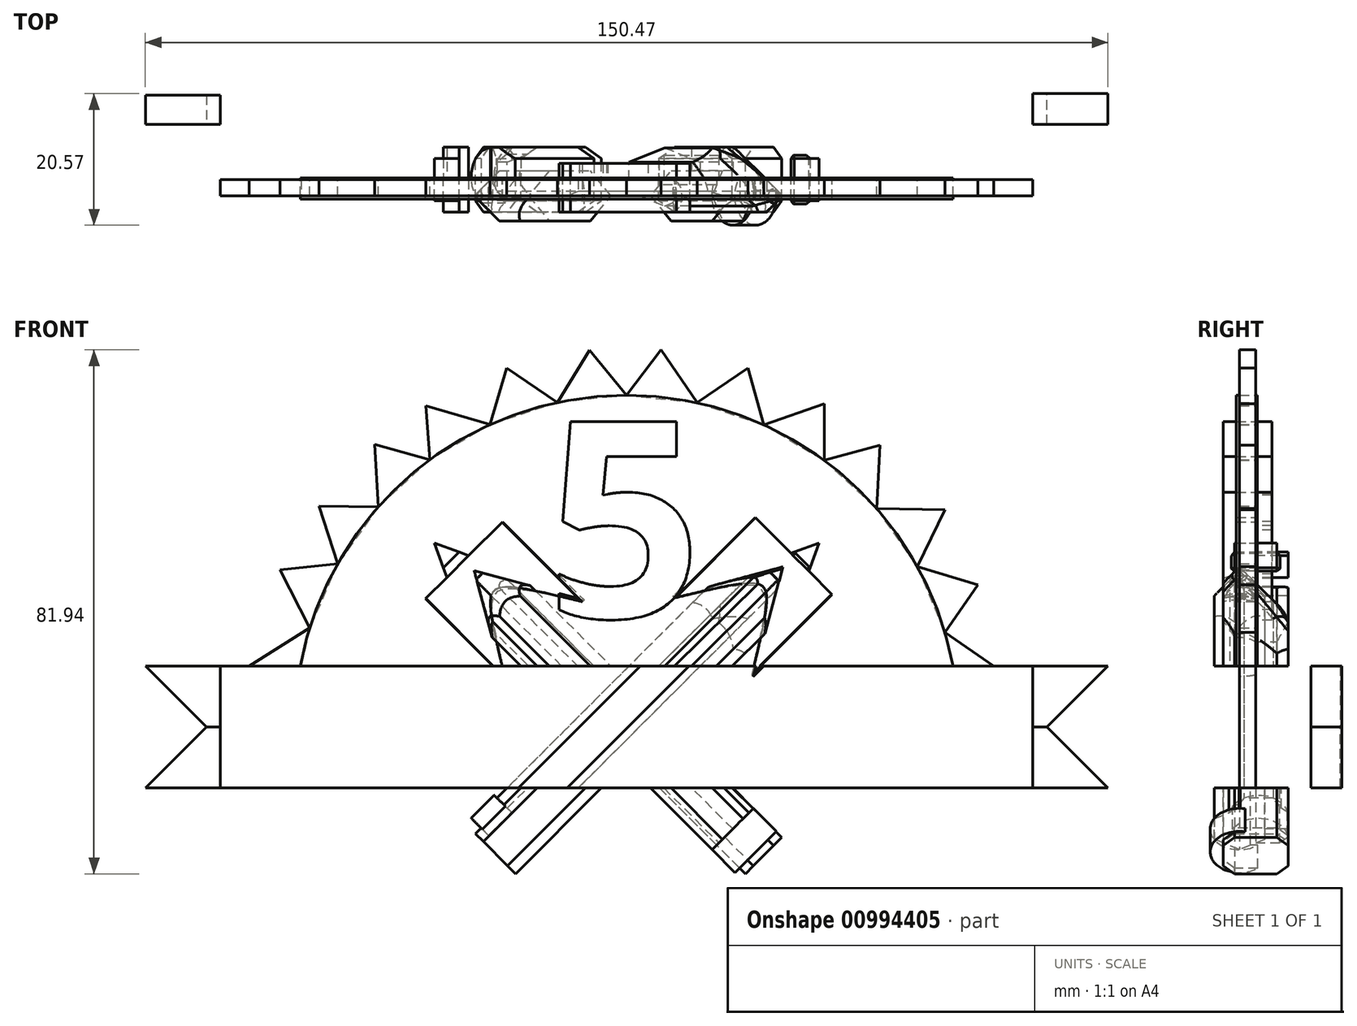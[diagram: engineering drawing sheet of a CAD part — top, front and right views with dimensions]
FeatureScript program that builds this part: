
annotation { "Feature Type Name" : "Feature", "Feature Type Description" : "" }
export const myFeature = defineFeature(function(context is Context, id is Id, definition is map)
    precondition{}
    {
        {
            var Q0;
            Q0=qCreatedBy(makeId("Front.planeOp"),FACE);
            var sketch = newSketch(context, id + "F0", { "sketchPlane" : qUnion([Q0])});
            skLineSegment(sketch, "E0.bottom", {"start": v(-63.5, 9.53) * mm, "end": v(63.5, 9.53) * mm});
            skLineSegment(sketch, "E0.top", {"start": v(-63.5, -9.52) * mm, "end": v(63.5, -9.52) * mm});
            skLineSegment(sketch, "E0.left", {"start": v(-63.5, 9.53) * mm, "end": v(-63.5, -9.52) * mm});
            skLineSegment(sketch, "E0.right", {"start": v(63.5, 9.53) * mm, "end": v(63.5, -9.52) * mm});
            skSolve(sketch);
        }
        {
            var Q0;
            Q0=qCreatedBy(makeId("Top.planeOp"),FACE);
            var sketch = newSketch(context, id + "F1", { "sketchPlane" : qUnion([Q0])});
            skLineSegment(sketch, "E1", {"start": v(-63.5, 0) * mm, "end": v(-57.46, 8.63) * mm});
            skLineSegment(sketch, "E2", {"start": v(-57.46, 8.63) * mm, "end": v(-42.22, 8.63) * mm});
            skLineSegment(sketch, "E3", {"start": v(-42.22, 8.63) * mm, "end": v(-48.26, 0) * mm});
            skLineSegment(sketch, "E4", {"start": v(-48.26, 0) * mm, "end": v(-63.5, 0) * mm});
            skSolve(sketch);
        }
        {
            var Q0;
            Q0=makeQuery(id+"F1.imprint","IMPRINT",FACE,{"disambiguationData":[TD([[makeQuery(id+"F1.imprint","IMPRINT",EDGE,{"derivedFrom":sQuery(id+"F1.wireOp",EDGE,"E1")}),-1.0]])]});
            extrude(context, id + "F2", {"entities" : qUnion([Q0]), "depth" : 9.52 * mm, "offsetDistance" : 25.4 * mm});
        }
        {
            var Q0;
            Q0=makeQuery(id+"F2.opExtrude","CAP_FACE",FACE,{"disambiguationData":[OSD([sQuery(id+"F1.wireOp",EDGE,"E1"),sQuery(id+"F1.wireOp",EDGE,"E2"),sQuery(id+"F1.wireOp",EDGE,"E3"),sQuery(id+"F1.wireOp",EDGE,"E4")])],"isStart":true});
            extrude(context, id + "F3", {"entities" : qUnion([Q0]), "depth" : 9.52 * mm, "offsetDistance" : 25.4 * mm});
        }
        {
            var Q0;
            Q0=qCreatedBy(makeId("Top.planeOp"),FACE);
            var sketch = newSketch(context, id + "F4", { "sketchPlane" : qUnion([Q0])});
            skLineSegment(sketch, "E5", {"start": v(63.5, 0) * mm, "end": v(57.45, 8.64) * mm});
            skLineSegment(sketch, "E6", {"start": v(57.45, 8.64) * mm, "end": v(42.21, 8.64) * mm});
            skLineSegment(sketch, "E7", {"start": v(42.21, 8.64) * mm, "end": v(48.26, 0) * mm});
            skLineSegment(sketch, "E8", {"start": v(48.26, 0) * mm, "end": v(63.5, 0) * mm});
            skSolve(sketch);
        }
        {
            var Q0;
            Q0 = qSketchRegion(id + "F4", true);
            extrude(context, id + "F5", {"entities" : qUnion([Q0]), "depth" : 9.52 * mm, "offsetDistance" : 25.4 * mm});
        }
        {
            var Q0;
            Q0=makeQuery(id+"F5.opExtrude","CAP_FACE",FACE,{"disambiguationData":[OSD([sQuery(id+"F4.wireOp",EDGE,"E5"),sQuery(id+"F4.wireOp",EDGE,"E6"),sQuery(id+"F4.wireOp",EDGE,"E7"),sQuery(id+"F4.wireOp",EDGE,"E8")])],"isStart":true});
            var Q1;
            Q1 = qSketchRegion(id + "F3emU6Rc3k6mnXg_5", true);
            extrude(context, id + "F6", {"entities" : qUnion([Q0, Q1]), "depth" : 9.52 * mm, "offsetDistance" : 25.4 * mm});
        }
        {
            var Q0;
            Q0=qCreatedBy(makeId("Front.planeOp"),FACE);
            var sketch = newSketch(context, id + "F7", { "sketchPlane" : qUnion([Q0])});
            skLineSegment(sketch, "E9", {"start": v(0, 0) * mm, "end": v(0, 56.19) * mm, "construction": true});
            skSolve(sketch);
        }
        {
            var Q0;
            Q0=makeQuery(id+"F0.imprint","IMPRINT",FACE,{"disambiguationData":[TD([[makeQuery(id+"F0.imprint","IMPRINT",EDGE,{"derivedFrom":sQuery(id+"F0.wireOp",EDGE,"E0.bottom")}),-1.0]])]});
            var sketch = newSketch(context, id + "F8", { "sketchPlane" : qUnion([Q0])});
            skArc(sketch, "E10", {"start": v(51.02, 9.53) * mm, "mid": v(0, 51.9) * mm, "end": v(-51.02, 9.52) * mm});
            skSolve(sketch);
        }
        {
            var Q0;
            {var subQ0=sQuery(id+"F8.wireOp",EDGE,"E10");Q0=makeQuery(id+"F8.imprint","IMPRINT",FACE,{"disambiguationData":[TD([[makeQuery(id+"F8.imprint","IMPRINT",EDGE,{"derivedFrom":subQ0}),1.0]])]});}
            extrude(context, id + "F9", {"entities" : qUnion([Q0]), "oppositeDirection" : true, "depth" : 0.25 * mm, "offsetDistance" : 25.4 * mm});
        }
        {
            var Q0;
            Q0=qCreatedBy(makeId("Front.planeOp"),FACE);
            var sketch = newSketch(context, id + "F10", { "sketchPlane" : qUnion([Q0])});
            skText(sketch, "E11", { "text": "5\n", "fontName": "OpenSans-Bold.ttf"});
            const initialGuessF10  = {"E11": [-0.01267, 0.01715, 1, 0, 0.03088]};
            skSetInitialGuess(sketch, initialGuessF10);
            skSolve(sketch);
        }
        {
            var Q0;
            Q0 = qSketchRegion(id + "F10", true);
            extrude(context, id + "F11", {"entities" : qUnion([Q0]), "depth" : 5.08 * mm, "offsetDistance" : 25.4 * mm});
        }
        {
            var Q0;
            Q0=qCreatedBy(makeId("Front.planeOp"),FACE);
            var sketch = newSketch(context, id + "F12", { "sketchPlane" : qUnion([Q0])});
            skText(sketch, "E12", { "text": "SoHacks", "fontName": "OpenSans-Bold.ttf"});
            const initialGuessF12  = {"E12": [-0.03987, -0.0065, 1, 0, 0.01368]};
            skSetInitialGuess(sketch, initialGuessF12);
            skSolve(sketch);
        }
        {
            var Q0;
            Q0 = qSketchRegion(id + "F12", true);
            extrude(context, id + "F13", {"entities" : qUnion([Q0]), "depth" : 5.08 * mm, "offsetDistance" : 25.4 * mm});
        }
        {
            var Q0;
            Q0=qCreatedBy(makeId("Top.planeOp"),FACE);
            var sketch = newSketch(context, id + "F14", { "sketchPlane" : qUnion([Q0])});
            skLineSegment(sketch, "E13.bottom", {"start": v(-42.22, 8.63) * mm, "end": v(-75.24, 8.63) * mm});
            skLineSegment(sketch, "E13.top", {"start": v(-42.22, 13.2) * mm, "end": v(-75.24, 13.2) * mm});
            skLineSegment(sketch, "E13.left", {"start": v(-42.22, 8.63) * mm, "end": v(-42.22, 13.2) * mm});
            skLineSegment(sketch, "E13.right", {"start": v(-75.24, 8.63) * mm, "end": v(-75.24, 13.2) * mm});
            skSolve(sketch);
        }
        {
            var Q0;
            Q0 = qSketchRegion(id + "F14", true);
            extrude(context, id + "F15", {"entities" : qUnion([Q0]), "depth" : 9.52 * mm, "offsetDistance" : 25.4 * mm});
        }
        {
            var Q0;
            Q0=makeQuery(id+"F15.opExtrude","CAP_FACE",FACE,{"disambiguationData":[OSD([sQuery(id+"F14.wireOp",EDGE,"E13.bottom"),sQuery(id+"F14.wireOp",EDGE,"E13.top"),sQuery(id+"F14.wireOp",EDGE,"E13.left"),sQuery(id+"F14.wireOp",EDGE,"E13.right")])],"isStart":true});
            extrude(context, id + "F16", {"entities" : qUnion([Q0]), "depth" : 9.52 * mm, "offsetDistance" : 25.4 * mm});
        }
        {
            var Q0;
            Q0=makeQuery(id+"F15.opExtrude","CAP_EDGE",EDGE,{"disambiguationData":[OSD([sQuery(id+"F14.wireOp",EDGE,"E13.right")])],"isStart":true});
            chamfer(context, id + "F17", {"entities" : qUnion([Q0]), "width" : 9.52 * mm, "tangentPropagation" : true});
        }
        {
            var Q0;
            Q0=makeQuery(id+"F16.opExtrude","CAP_EDGE",EDGE,{"disambiguationData":[OSD([sQuery(id+"F14.wireOp",EDGE,"E13.right")])],"isStart":true});
            chamfer(context, id + "F18", {"entities" : qUnion([Q0]), "width" : 9.52 * mm, "tangentPropagation" : true});
        }
        {
            var Q0;
            Q0=qCreatedBy(makeId("Top.planeOp"),FACE);
            var sketch = newSketch(context, id + "F19", { "sketchPlane" : qUnion([Q0])});
            skLineSegment(sketch, "E14.bottom", {"start": v(42.21, 8.64) * mm, "end": v(75.23, 8.64) * mm});
            skLineSegment(sketch, "E14.top", {"start": v(42.21, 13.46) * mm, "end": v(75.23, 13.46) * mm});
            skLineSegment(sketch, "E14.left", {"start": v(42.21, 8.64) * mm, "end": v(42.21, 13.46) * mm});
            skLineSegment(sketch, "E14.right", {"start": v(75.23, 8.64) * mm, "end": v(75.23, 13.46) * mm});
            skSolve(sketch);
        }
        {
            var Q0;
            Q0=makeQuery(id+"F19.imprint","IMPRINT",FACE,{"disambiguationData":[TD([[makeQuery(id+"F19.imprint","IMPRINT",EDGE,{"derivedFrom":sQuery(id+"F19.wireOp",EDGE,"E14.bottom")}),1.0]])]});
            extrude(context, id + "F20", {"entities" : qUnion([Q0]), "depth" : 9.52 * mm, "offsetDistance" : 25.4 * mm});
        }
        {
            var Q0;
            Q0 = qSketchRegion(id + "F19", true);
            extrude(context, id + "F21", {"entities" : qUnion([Q0]), "oppositeDirection" : true, "depth" : 9.52 * mm, "offsetDistance" : 25.4 * mm});
        }
        {
            var Q0;
            Q0=makeQuery(id+"F20.opExtrude","CAP_EDGE",EDGE,{"disambiguationData":[OSD([sQuery(id+"F19.wireOp",EDGE,"E14.right")])],"isStart":true});
            chamfer(context, id + "F22", {"entities" : qUnion([Q0]), "width" : 9.52 * mm, "tangentPropagation" : true});
        }
        {
            var Q0;
            Q0=makeQuery(id+"F21.opExtrude","CAP_EDGE",EDGE,{"disambiguationData":[OSD([sQuery(id+"F19.wireOp",EDGE,"E14.right")])],"isStart":true});
            chamfer(context, id + "F23", {"entities" : qUnion([Q0]), "width" : 9.52 * mm, "tangentPropagation" : true});
        }
        {
            var Q0;
            Q0=qCreatedBy(makeId("Front.planeOp"),FACE);
            var sketch = newSketch(context, id + "F24", { "sketchPlane" : qUnion([Q0])});
            skLineSegment(sketch, "E15", {"start": v(0, 0) * mm, "end": v(0, 9.53) * mm, "construction": true});
            skLineSegment(sketch, "E16", {"start": v(0, 9.53) * mm, "end": v(-10.16, 9.53) * mm, "construction": true});
            skLineSegment(sketch, "E17", {"start": v(0, 9.53) * mm, "end": v(10.16, 9.53) * mm, "construction": true});
            skLineSegment(sketch, "E18", {"start": v(-10.16, 9.53) * mm, "end": v(-16.51, 9.53) * mm, "construction": true});
            skLineSegment(sketch, "E19", {"start": v(10.16, 9.53) * mm, "end": v(16.51, 9.53) * mm, "construction": true});
            skLineSegment(sketch, "E20", {"start": v(0, 0) * mm, "end": v(0, -9.52) * mm, "construction": true});
            skLineSegment(sketch, "E21", {"start": v(0, -9.52) * mm, "end": v(-10.16, -9.52) * mm, "construction": true});
            skLineSegment(sketch, "E22", {"start": v(-10.16, -9.52) * mm, "end": v(-16.51, -9.52) * mm, "construction": true});
            skLineSegment(sketch, "E23", {"start": v(0, -9.52) * mm, "end": v(10.16, -9.52) * mm, "construction": true});
            skLineSegment(sketch, "E24", {"start": v(10.16, -9.52) * mm, "end": v(16.51, -9.52) * mm, "construction": true});
            skSolve(sketch);
        }
        {
            var Q0;
            Q0=qCreatedBy(makeId("Front.planeOp"),FACE);
            var sketch = newSketch(context, id + "F25", { "sketchPlane" : qUnion([Q0])});
            skLineSegment(sketch, "E25", {"start": v(-10.16, 9.52) * mm, "end": v(-23.63, 23) * mm});
            skLineSegment(sketch, "E26", {"start": v(-23.63, 23) * mm, "end": v(-26.8, 19.82) * mm});
            skLineSegment(sketch, "E27", {"start": v(-26.8, 19.82) * mm, "end": v(-16.51, 9.52) * mm});
            skLineSegment(sketch, "E28", {"start": v(10.16, 9.52) * mm, "end": v(23.63, 23) * mm});
            skLineSegment(sketch, "E29", {"start": v(23.63, 23) * mm, "end": v(26.8, 19.82) * mm});
            skLineSegment(sketch, "E30", {"start": v(26.8, 19.82) * mm, "end": v(16.5, 9.53) * mm});
            skLineSegment(sketch, "E31", {"start": v(-10.16, 9.52) * mm, "end": v(-16.51, 9.52) * mm});
            skLineSegment(sketch, "E32", {"start": v(10.16, 9.52) * mm, "end": v(16.5, 9.53) * mm});
            skSolve(sketch);
        }
        {
            var Q0;
            Q0 = qSketchRegion(id + "F25", true);
            extrude(context, id + "F26", {"entities" : qUnion([Q0]), "depth" : 5.08 * mm, "offsetDistance" : 25.4 * mm});
        }
        {
            var Q0;
            Q0=qCreatedBy(makeId("Front.planeOp"),FACE);
            var sketch = newSketch(context, id + "F27", { "sketchPlane" : qUnion([Q0])});
            skLineSegment(sketch, "E33", {"start": v(23.63, 23) * mm, "end": v(21.13, 25.52) * mm});
            skLineSegment(sketch, "E34", {"start": v(21.13, 25.52) * mm, "end": v(4.97, 9.52) * mm});
            skLineSegment(sketch, "E35", {"start": v(4.97, 9.53) * mm, "end": v(10.16, 9.53) * mm});
            skLineSegment(sketch, "E36", {"start": v(10.16, 9.52) * mm, "end": v(23.63, 23) * mm});
            skLineSegment(sketch, "E37", {"start": v(-23.63, 23) * mm, "end": v(-21.12, 25.5) * mm});
            skLineSegment(sketch, "E38", {"start": v(-21.12, 25.5) * mm, "end": v(-5.13, 9.52) * mm});
            skLineSegment(sketch, "E39", {"start": v(-5.13, 9.53) * mm, "end": v(-10.16, 9.53) * mm});
            skLineSegment(sketch, "E40", {"start": v(-10.16, 9.52) * mm, "end": v(-23.63, 23) * mm});
            skSolve(sketch);
        }
        {
            var Q0;
            Q0 = qSketchRegion(id + "F27", true);
            extrude(context, id + "F28", {"entities" : qUnion([Q0]), "depth" : 5.08 * mm, "offsetDistance" : 25.4 * mm});
        }
        {
            var Q0;
            Q0=qCreatedBy(makeId("Front.planeOp"),FACE);
            var sketch = newSketch(context, id + "F29", { "sketchPlane" : qUnion([Q0])});
            skLineSegment(sketch, "E41", {"start": v(-26.8, 19.82) * mm, "end": v(-30.06, 28.77) * mm, "construction": true});
            skLineSegment(sketch, "E42", {"start": v(-30.06, 28.77) * mm, "end": v(-21.12, 25.5) * mm, "construction": true});
            skLineSegment(sketch, "E43", {"start": v(-21.12, 25.5) * mm, "end": v(-26.8, 19.82) * mm, "construction": true});
            skLineSegment(sketch, "E44", {"start": v(21.13, 25.52) * mm, "end": v(26.8, 19.82) * mm, "construction": true});
            skLineSegment(sketch, "E45", {"start": v(26.8, 19.82) * mm, "end": v(30.08, 28.76) * mm, "construction": true});
            skLineSegment(sketch, "E46", {"start": v(30.08, 28.76) * mm, "end": v(21.13, 25.52) * mm, "construction": true});
            skSolve(sketch);
        }
        {
            var Q0;
            Q0=qCreatedBy(makeId("Front.planeOp"),FACE);
            var sketch = newSketch(context, id + "F30", { "sketchPlane" : qUnion([Q0])});
            skLineSegment(sketch, "E47", {"start": v(21.13, 25.52) * mm, "end": v(26.2, 27.36) * mm});
            skLineSegment(sketch, "E48", {"start": v(26.2, 27.36) * mm, "end": v(28.66, 24.9) * mm});
            skLineSegment(sketch, "E49", {"start": v(28.66, 24.9) * mm, "end": v(26.8, 19.82) * mm});
            skLineSegment(sketch, "E50", {"start": v(26.8, 19.82) * mm, "end": v(21.13, 25.52) * mm});
            skLineSegment(sketch, "E51", {"start": v(-26.8, 19.82) * mm, "end": v(-21.12, 25.5) * mm});
            skLineSegment(sketch, "E52", {"start": v(-21.12, 25.5) * mm, "end": v(-26.2, 27.36) * mm});
            skLineSegment(sketch, "E53", {"start": v(-26.2, 27.36) * mm, "end": v(-28.65, 24.9) * mm});
            skLineSegment(sketch, "E54", {"start": v(-28.65, 24.9) * mm, "end": v(-26.8, 19.82) * mm});
            skSolve(sketch);
        }
        {
            var Q0;
            Q0 = qSketchRegion(id + "F30", true);
            extrude(context, id + "F31", {"entities" : qUnion([Q0]), "depth" : 5.08 * mm, "offsetDistance" : 25.4 * mm});
        }
        {
            var Q0;
            Q0=qCreatedBy(makeId("Front.planeOp"),FACE);
            var sketch = newSketch(context, id + "F32", { "sketchPlane" : qUnion([Q0])});
            skLineSegment(sketch, "E55", {"start": v(26.2, 27.36) * mm, "end": v(28.66, 24.9) * mm});
            skLineSegment(sketch, "E56", {"start": v(28.66, 24.9) * mm, "end": v(30.08, 28.76) * mm});
            skLineSegment(sketch, "E57", {"start": v(30.08, 28.76) * mm, "end": v(26.2, 27.36) * mm});
            skLineSegment(sketch, "E58", {"start": v(-28.65, 24.9) * mm, "end": v(-26.2, 27.36) * mm});
            skLineSegment(sketch, "E59", {"start": v(-26.2, 27.36) * mm, "end": v(-30.06, 28.77) * mm});
            skLineSegment(sketch, "E60", {"start": v(-30.06, 28.77) * mm, "end": v(-28.65, 24.9) * mm});
            skSolve(sketch);
        }
        {
            var Q0;
            Q0 = qSketchRegion(id + "F32", true);
            extrude(context, id + "F33", {"entities" : qUnion([Q0]), "depth" : 3.3 * mm, "offsetDistance" : 25.4 * mm});
        }
        {
            var Q0;
            Q0=qCreatedBy(makeId("Front.planeOp"),FACE);
            var sketch = newSketch(context, id + "F34", { "sketchPlane" : qUnion([Q0])});
            skLineSegment(sketch, "E61", {"start": v(16.51, -9.52) * mm, "end": v(24.25, -17.26) * mm});
            skLineSegment(sketch, "E62", {"start": v(24.25, -17.26) * mm, "end": v(21.07, -20.44) * mm});
            skLineSegment(sketch, "E63", {"start": v(21.07, -20.44) * mm, "end": v(10.16, -9.52) * mm});
            skLineSegment(sketch, "E64", {"start": v(10.16, -9.52) * mm, "end": v(16.51, -9.52) * mm});
            skLineSegment(sketch, "E65", {"start": v(-16.52, -9.52) * mm, "end": v(-10.16, -9.52) * mm});
            skLineSegment(sketch, "E66", {"start": v(-10.16, -9.52) * mm, "end": v(-20.48, -19.85) * mm});
            skLineSegment(sketch, "E67", {"start": v(-20.48, -19.85) * mm, "end": v(-23.66, -16.67) * mm});
            skLineSegment(sketch, "E68", {"start": v(-23.66, -16.67) * mm, "end": v(-16.52, -9.52) * mm});
            skSolve(sketch);
        }
        {
            var Q0;
            Q0 = qSketchRegion(id + "F34", true);
            extrude(context, id + "F35", {"entities" : qUnion([Q0]), "depth" : 5.08 * mm, "offsetDistance" : 25.4 * mm});
        }
        {
            var Q0;
            Q0=qCreatedBy(makeId("Front.planeOp"),FACE);
            var sketch = newSketch(context, id + "F36", { "sketchPlane" : qUnion([Q0])});
            skLineSegment(sketch, "E69", {"start": v(-20.48, -19.85) * mm, "end": v(-17.38, -22.95) * mm});
            skLineSegment(sketch, "E70", {"start": v(-17.38, -22.95) * mm, "end": v(-3.95, -9.52) * mm});
            skLineSegment(sketch, "E71", {"start": v(-3.95, -9.52) * mm, "end": v(-10.16, -9.52) * mm});
            skLineSegment(sketch, "E72", {"start": v(-10.16, -9.53) * mm, "end": v(-20.48, -19.85) * mm});
            skLineSegment(sketch, "E73", {"start": v(10.16, -9.52) * mm, "end": v(5.13, -9.52) * mm});
            skLineSegment(sketch, "E74", {"start": v(5.13, -9.52) * mm, "end": v(18.56, -22.95) * mm});
            skLineSegment(sketch, "E75", {"start": v(18.56, -22.95) * mm, "end": v(21.07, -20.44) * mm});
            skLineSegment(sketch, "E76", {"start": v(21.07, -20.44) * mm, "end": v(10.16, -9.52) * mm});
            skSolve(sketch);
        }
        {
            var Q0;
            Q0=makeQuery(id+"F35.opExtrude","SWEPT_FACE",FACE,{"disambiguationData":[OSD([sQuery(id+"F34.wireOp",EDGE,"E62")])]});
            cPlane(context, id + "F37", {"entities" : qUnion([Q0]), "cplaneType" : CPlaneType.OFFSET, "offset" : 0 * mm, "width" : 152.4 * mm, "height" : 152.4 * mm});
        }
        {
            var Q0;
            Q0=qCreatedBy(id+"F37.planeOp",FACE);
            var sketch = newSketch(context, id + "F38", { "sketchPlane" : qUnion([Q0])});
            skCircle(sketch, "E77.cCircle", {"center": v(-2.54, 0.45) * mm, "radius": 3.94 * mm, "construction": true});
            skLineSegment(sketch, "E77.0", {"start": v(-6.48, 2.72) * mm, "end": v(-2.54, 5) * mm});
            skLineSegment(sketch, "E77.1", {"start": v(-2.54, 5) * mm, "end": v(1.4, 2.72) * mm});
            skLineSegment(sketch, "E77.2", {"start": v(1.4, 2.72) * mm, "end": v(1.4, -1.82) * mm});
            skLineSegment(sketch, "E77.3", {"start": v(1.4, -1.82) * mm, "end": v(-2.54, -4.1) * mm});
            skLineSegment(sketch, "E77.4", {"start": v(-2.54, -4.1) * mm, "end": v(-6.48, -1.82) * mm});
            skLineSegment(sketch, "E77.5", {"start": v(-6.48, -1.82) * mm, "end": v(-6.48, 2.72) * mm});
            skPoint(sketch, "E77.0.midPoint", {"position": v(-4.5, 3.86) * mm});
            skSolve(sketch);
        }
        {
            var Q0;
            Q0=makeQuery(id+"F38.imprint","IMPRINT",FACE,{"disambiguationData":[TD([[makeQuery(id+"F38.imprint","IMPRINT",EDGE,{"derivedFrom":sQuery(id+"F38.wireOp",EDGE,"E77.0")}),-1.0]])]});
            extrude(context, id + "F39", {"entities" : qUnion([Q0]), "oppositeDirection" : true, "depth" : 63.5 * mm, "offsetDistance" : 25.4 * mm, "hasSecondDirection" : true, "secondDirectionOppositeDirection" : true, "secondDirectionDepth" : 6.35 * mm});
        }
        {
            var Q0;
            Q0=makeQuery(id+"F39.opExtrude","SWEPT_FACE",FACE,{"disambiguationData":[OSD([sQuery(id+"F38.wireOp",EDGE,"E77.2")])]});
            var Q1;
            Q1=makeQuery(id+"F39.opExtrude","SWEPT_FACE",FACE,{"disambiguationData":[OSD([sQuery(id+"F38.wireOp",EDGE,"E77.5")])]});
            cPlane(context, id + "F40", {"entities" : qUnion([Q0, Q1]), "cplaneType" : CPlaneType.MID_PLANE, "offset" : 25.4 * mm, "oppositeDirection" : true, "width" : 152.4 * mm, "height" : 152.4 * mm});
        }
        {
            var Q0;
            Q0=qCreatedBy(id+"F40.planeOp",FACE);
            var sketch = newSketch(context, id + "F41", { "sketchPlane" : qUnion([Q0])});
            skLineSegment(sketch, "E78", {"start": v(23.83, 24.46) * mm, "end": v(6.65, 19.86) * mm});
            skLineSegment(sketch, "E79", {"start": v(6.65, 19.86) * mm, "end": v(19.16, 32.36) * mm});
            skLineSegment(sketch, "E80", {"start": v(25.44, 26.08) * mm, "end": v(19.16, 32.36) * mm});
            skLineSegment(sketch, "E81", {"start": v(23.83, 24.46) * mm, "end": v(16.64, 17.28) * mm, "construction": true});
            skLineSegment(sketch, "E82", {"start": v(25.44, 26.08) * mm, "end": v(23.83, 24.46) * mm});
            skSolve(sketch);
        }
        {
            var Q0;
            Q0=makeQuery(id+"F41.imprint","IMPRINT",FACE,{"disambiguationData":[TD([[makeQuery(id+"F41.imprint","IMPRINT",EDGE,{"derivedFrom":sQuery(id+"F41.wireOp",EDGE,"E78")}),-1.0]])]});
            var Q1;
            Q1=sQuery(id+"F41.wireOp",EDGE,"E81");
            revolve(context, id + "F42", {"operationType" : NewBodyOperationType.REMOVE, "surfaceOperationType" : NewSurfaceOperationType.NEW, "entities" : qUnion([Q0]), "axis" : qUnion([Q1]), "revolveType" : RevolveType.FULL, "oppositeDirection" : true});
        }
        {
            var Q0;
            Q0 = qSketchRegion(id + "F36", true);
            extrude(context, id + "F43", {"entities" : qUnion([Q0]), "depth" : 5.08 * mm, "offsetDistance" : 25.4 * mm});
        }
        {
            var Q0;
            Q0=qCreatedBy(makeId("Front.planeOp"),FACE);
            var sketch = newSketch(context, id + "F44", { "sketchPlane" : qUnion([Q0])});
            skLineSegment(sketch, "E83", {"start": v(0, 51.9) * mm, "end": v(-10.8, 50.77) * mm});
            skLineSegment(sketch, "E84", {"start": v(-10.8, 50.77) * mm, "end": v(-21.34, 47.31) * mm});
            skLineSegment(sketch, "E85", {"start": v(-21.34, 47.31) * mm, "end": v(-30.77, 41.8) * mm});
            skLineSegment(sketch, "E86", {"start": v(-30.77, 41.8) * mm, "end": v(-38.83, 34.43) * mm});
            skLineSegment(sketch, "E87", {"start": v(-38.83, 34.43) * mm, "end": v(-45.18, 25.54) * mm});
            skLineSegment(sketch, "E88", {"start": v(-45.18, 25.54) * mm, "end": v(-49.52, 15.52) * mm});
            skLineSegment(sketch, "E89", {"start": v(-49.52, 15.52) * mm, "end": v(-50.93, 9.33) * mm});
            skLineSegment(sketch, "E90", {"start": v(-50.93, 9.33) * mm, "end": v(-59.34, 9.33) * mm});
            skLineSegment(sketch, "E91", {"start": v(-59.34, 9.33) * mm, "end": v(-49.52, 15.52) * mm});
            skLineSegment(sketch, "E92", {"start": v(-49.52, 15.52) * mm, "end": v(-54.21, 24.57) * mm});
            skLineSegment(sketch, "E93", {"start": v(-54.21, 24.57) * mm, "end": v(-45.18, 25.54) * mm});
            skLineSegment(sketch, "E94", {"start": v(-45.18, 25.54) * mm, "end": v(-48.1, 34.56) * mm});
            skLineSegment(sketch, "E95", {"start": v(-48.1, 34.56) * mm, "end": v(-38.83, 34.43) * mm});
            skLineSegment(sketch, "E96", {"start": v(-30.77, 41.8) * mm, "end": v(-39.42, 44.22) * mm});
            skLineSegment(sketch, "E97", {"start": v(-39.42, 44.22) * mm, "end": v(-38.83, 34.43) * mm});
            skLineSegment(sketch, "E98", {"start": v(-30.77, 41.8) * mm, "end": v(-31.4, 50.25) * mm});
            skLineSegment(sketch, "E99", {"start": v(-31.4, 50.25) * mm, "end": v(-21.34, 47.31) * mm});
            skLineSegment(sketch, "E100", {"start": v(-21.34, 47.31) * mm, "end": v(-18.75, 56.18) * mm});
            skLineSegment(sketch, "E101", {"start": v(-18.75, 56.18) * mm, "end": v(-10.8, 50.77) * mm});
            skLineSegment(sketch, "E102", {"start": v(-10.8, 50.77) * mm, "end": v(-5.83, 58.95) * mm});
            skLineSegment(sketch, "E103", {"start": v(-5.83, 58.95) * mm, "end": v(0, 51.9) * mm});
            skLineSegment(sketch, "E104", {"start": v(0, 51.9) * mm, "end": v(11.01, 50.72) * mm});
            skLineSegment(sketch, "E105", {"start": v(11.01, 50.72) * mm, "end": v(21.45, 47.26) * mm});
            skLineSegment(sketch, "E106", {"start": v(21.45, 47.26) * mm, "end": v(30.9, 41.7) * mm});
            skLineSegment(sketch, "E107", {"start": v(30.9, 41.7) * mm, "end": v(39.06, 34.17) * mm});
            skLineSegment(sketch, "E108", {"start": v(39.06, 34.17) * mm, "end": v(45.43, 25.1) * mm});
            skLineSegment(sketch, "E109", {"start": v(45.43, 25.1) * mm, "end": v(49.74, 14.81) * mm});
            skLineSegment(sketch, "E110", {"start": v(49.74, 14.81) * mm, "end": v(51.02, 9.52) * mm});
            skLineSegment(sketch, "E111", {"start": v(51.02, 9.53) * mm, "end": v(57.35, 9.53) * mm});
            skLineSegment(sketch, "E112", {"start": v(57.35, 9.52) * mm, "end": v(49.74, 14.81) * mm});
            skLineSegment(sketch, "E113", {"start": v(49.74, 14.81) * mm, "end": v(54.9, 22.23) * mm});
            skLineSegment(sketch, "E114", {"start": v(54.9, 22.23) * mm, "end": v(45.43, 25.1) * mm});
            skLineSegment(sketch, "E115", {"start": v(45.43, 25.1) * mm, "end": v(49.74, 33.99) * mm});
            skLineSegment(sketch, "E116", {"start": v(49.74, 33.99) * mm, "end": v(39.06, 34.17) * mm});
            skLineSegment(sketch, "E117", {"start": v(39.06, 34.17) * mm, "end": v(39.58, 44.06) * mm});
            skLineSegment(sketch, "E118", {"start": v(39.58, 44.06) * mm, "end": v(30.9, 41.7) * mm});
            skLineSegment(sketch, "E119", {"start": v(30.9, 50.55) * mm, "end": v(21.45, 47.26) * mm});
            skLineSegment(sketch, "E120", {"start": v(30.9, 50.55) * mm, "end": v(30.9, 41.7) * mm});
            skLineSegment(sketch, "E121", {"start": v(21.45, 47.26) * mm, "end": v(18.95, 56.12) * mm});
            skLineSegment(sketch, "E122", {"start": v(18.95, 56.12) * mm, "end": v(11.01, 50.72) * mm});
            skLineSegment(sketch, "E123", {"start": v(11.01, 50.72) * mm, "end": v(5.39, 58.99) * mm});
            skLineSegment(sketch, "E124", {"start": v(5.39, 58.99) * mm, "end": v(0, 51.9) * mm});
            skSolve(sketch);
        }
        {
            var Q0;
            Q0=makeQuery(id+"F44.imprint","IMPRINT",FACE,{"disambiguationData":[TD([[makeQuery(id+"F44.imprint","IMPRINT",EDGE,{"derivedFrom":sQuery(id+"F44.wireOp",EDGE,"E86")}),-1.0]])]});
            var Q1;
            Q1=makeQuery(id+"F44.imprint","IMPRINT",FACE,{"disambiguationData":[TD([[makeQuery(id+"F44.imprint","IMPRINT",EDGE,{"derivedFrom":sQuery(id+"F44.wireOp",EDGE,"E85")}),-1.0]])]});
            var Q2;
            Q2=makeQuery(id+"F44.imprint","IMPRINT",FACE,{"disambiguationData":[TD([[makeQuery(id+"F44.imprint","IMPRINT",EDGE,{"derivedFrom":sQuery(id+"F44.wireOp",EDGE,"E84")}),-1.0]])]});
            var Q3;
            Q3=makeQuery(id+"F44.imprint","IMPRINT",FACE,{"disambiguationData":[TD([[makeQuery(id+"F44.imprint","IMPRINT",EDGE,{"derivedFrom":sQuery(id+"F44.wireOp",EDGE,"E83")}),-1.0]])]});
            var Q4;
            Q4=makeQuery(id+"F44.imprint","IMPRINT",FACE,{"disambiguationData":[TD([[makeQuery(id+"F44.imprint","IMPRINT",EDGE,{"derivedFrom":sQuery(id+"F44.wireOp",EDGE,"E87")}),-1.0]])]});
            var Q5;
            Q5=makeQuery(id+"F44.imprint","IMPRINT",FACE,{"disambiguationData":[TD([[makeQuery(id+"F44.imprint","IMPRINT",EDGE,{"derivedFrom":sQuery(id+"F44.wireOp",EDGE,"E88")}),-1.0]])]});
            var Q6;
            Q6=makeQuery(id+"F44.imprint","IMPRINT",FACE,{"disambiguationData":[TD([[makeQuery(id+"F44.imprint","IMPRINT",EDGE,{"derivedFrom":sQuery(id+"F44.wireOp",EDGE,"E89")}),-1.0]])]});
            var Q7;
            Q7=makeQuery(id+"F44.imprint","IMPRINT",FACE,{"disambiguationData":[TD([[makeQuery(id+"F44.imprint","IMPRINT",EDGE,{"derivedFrom":sQuery(id+"F44.wireOp",EDGE,"E104")}),1.0]])]});
            var Q8;
            Q8=makeQuery(id+"F44.imprint","IMPRINT",FACE,{"disambiguationData":[TD([[makeQuery(id+"F44.imprint","IMPRINT",EDGE,{"derivedFrom":sQuery(id+"F44.wireOp",EDGE,"E105")}),1.0]])]});
            var Q9;
            Q9=makeQuery(id+"F44.imprint","IMPRINT",FACE,{"disambiguationData":[TD([[makeQuery(id+"F44.imprint","IMPRINT",EDGE,{"derivedFrom":sQuery(id+"F44.wireOp",EDGE,"E106")}),1.0]])]});
            var Q10;
            Q10=makeQuery(id+"F44.imprint","IMPRINT",FACE,{"disambiguationData":[TD([[makeQuery(id+"F44.imprint","IMPRINT",EDGE,{"derivedFrom":sQuery(id+"F44.wireOp",EDGE,"E107")}),1.0]])]});
            var Q11;
            Q11=makeQuery(id+"F44.imprint","IMPRINT",FACE,{"disambiguationData":[TD([[makeQuery(id+"F44.imprint","IMPRINT",EDGE,{"derivedFrom":sQuery(id+"F44.wireOp",EDGE,"E108")}),1.0]])]});
            var Q12;
            Q12=makeQuery(id+"F44.imprint","IMPRINT",FACE,{"disambiguationData":[TD([[makeQuery(id+"F44.imprint","IMPRINT",EDGE,{"derivedFrom":sQuery(id+"F44.wireOp",EDGE,"E109")}),1.0]])]});
            var Q13;
            Q13=makeQuery(id+"F44.imprint","IMPRINT",FACE,{"disambiguationData":[TD([[makeQuery(id+"F44.imprint","IMPRINT",EDGE,{"derivedFrom":sQuery(id+"F44.wireOp",EDGE,"E110")}),1.0]])]});
            extrude(context, id + "F45", {"entities" : qUnion([Q0, Q1, Q2, Q3, Q4, Q5, Q6, Q7, Q8, Q9, Q10, Q11, Q12, Q13]), "depth" : 2.54 * mm, "offsetDistance" : 25.4 * mm});
        }
        {
            var Q0;
            Q0=makeQuery(id+"F11.opExtrude","CAP_FACE",FACE,{"disambiguationData":[OSD([sQuery(id+"F10.wireOp",EDGE,"E11.sketch_text.stroke-0"),sQuery(id+"F10.wireOp",EDGE,"E11.sketch_text.stroke-1"),sQuery(id+"F10.wireOp",EDGE,"E11.sketch_text.stroke-2"),sQuery(id+"F10.wireOp",EDGE,"E11.sketch_text.stroke-3"),sQuery(id+"F10.wireOp",EDGE,"E11.sketch_text.stroke-4"),sQuery(id+"F10.wireOp",EDGE,"E11.sketch_text.stroke-5"),sQuery(id+"F10.wireOp",EDGE,"E11.sketch_text.stroke-6"),sQuery(id+"F10.wireOp",EDGE,"E11.sketch_text.stroke-7"),sQuery(id+"F10.wireOp",EDGE,"E11.sketch_text.stroke-8"),sQuery(id+"F10.wireOp",EDGE,"E11.sketch_text.stroke-9"),sQuery(id+"F10.wireOp",EDGE,"E11.sketch_text.stroke-10"),sQuery(id+"F10.wireOp",EDGE,"E11.sketch_text.stroke-11"),sQuery(id+"F10.wireOp",EDGE,"E11.sketch_text.stroke-12"),sQuery(id+"F10.wireOp",EDGE,"E11.sketch_text.stroke-13"),sQuery(id+"F10.wireOp",EDGE,"E11.sketch_text.stroke-14"),sQuery(id+"F10.wireOp",EDGE,"E11.sketch_text.stroke-15"),sQuery(id+"F10.wireOp",EDGE,"E11.sketch_text.stroke-16"),sQuery(id+"F10.wireOp",EDGE,"E11.sketch_text.stroke-17")])],"isStart":true});
            var Q1;
            Q1=makeQuery(id+"F13.opExtrude","CAP_FACE",FACE,{"disambiguationData":[OSD([sQuery(id+"F12.wireOp",EDGE,"E12.sketch_text.stroke-0"),sQuery(id+"F12.wireOp",EDGE,"E12.sketch_text.stroke-1"),sQuery(id+"F12.wireOp",EDGE,"E12.sketch_text.stroke-2"),sQuery(id+"F12.wireOp",EDGE,"E12.sketch_text.stroke-3"),sQuery(id+"F12.wireOp",EDGE,"E12.sketch_text.stroke-4"),sQuery(id+"F12.wireOp",EDGE,"E12.sketch_text.stroke-5"),sQuery(id+"F12.wireOp",EDGE,"E12.sketch_text.stroke-6"),sQuery(id+"F12.wireOp",EDGE,"E12.sketch_text.stroke-7"),sQuery(id+"F12.wireOp",EDGE,"E12.sketch_text.stroke-8"),sQuery(id+"F12.wireOp",EDGE,"E12.sketch_text.stroke-9"),sQuery(id+"F12.wireOp",EDGE,"E12.sketch_text.stroke-10"),sQuery(id+"F12.wireOp",EDGE,"E12.sketch_text.stroke-11"),sQuery(id+"F12.wireOp",EDGE,"E12.sketch_text.stroke-12"),sQuery(id+"F12.wireOp",EDGE,"E12.sketch_text.stroke-13"),sQuery(id+"F12.wireOp",EDGE,"E12.sketch_text.stroke-14"),sQuery(id+"F12.wireOp",EDGE,"E12.sketch_text.stroke-15"),sQuery(id+"F12.wireOp",EDGE,"E12.sketch_text.stroke-16"),sQuery(id+"F12.wireOp",EDGE,"E12.sketch_text.stroke-17"),sQuery(id+"F12.wireOp",EDGE,"E12.sketch_text.stroke-18"),sQuery(id+"F12.wireOp",EDGE,"E12.sketch_text.stroke-19"),sQuery(id+"F12.wireOp",EDGE,"E12.sketch_text.stroke-20"),sQuery(id+"F12.wireOp",EDGE,"E12.sketch_text.stroke-21"),sQuery(id+"F12.wireOp",EDGE,"E12.sketch_text.stroke-22"),sQuery(id+"F12.wireOp",EDGE,"E12.sketch_text.stroke-23"),sQuery(id+"F12.wireOp",EDGE,"E12.sketch_text.stroke-24"),sQuery(id+"F12.wireOp",EDGE,"E12.sketch_text.stroke-25"),sQuery(id+"F12.wireOp",EDGE,"E12.sketch_text.stroke-26"),sQuery(id+"F12.wireOp",EDGE,"E12.sketch_text.stroke-27")])],"isStart":true});
            var Q2;
            Q2=makeQuery(id+"F13.opExtrude","CAP_FACE",FACE,{"disambiguationData":[OSD([sQuery(id+"F12.wireOp",EDGE,"E12.sketch_text.stroke-28"),sQuery(id+"F12.wireOp",EDGE,"E12.sketch_text.stroke-29"),sQuery(id+"F12.wireOp",EDGE,"E12.sketch_text.stroke-30"),sQuery(id+"F12.wireOp",EDGE,"E12.sketch_text.stroke-31"),sQuery(id+"F12.wireOp",EDGE,"E12.sketch_text.stroke-32"),sQuery(id+"F12.wireOp",EDGE,"E12.sketch_text.stroke-33"),sQuery(id+"F12.wireOp",EDGE,"E12.sketch_text.stroke-34"),sQuery(id+"F12.wireOp",EDGE,"E12.sketch_text.stroke-35"),sQuery(id+"F12.wireOp",EDGE,"E12.sketch_text.stroke-36"),sQuery(id+"F12.wireOp",EDGE,"E12.sketch_text.stroke-37"),sQuery(id+"F12.wireOp",EDGE,"E12.sketch_text.stroke-38"),sQuery(id+"F12.wireOp",EDGE,"E12.sketch_text.stroke-39"),sQuery(id+"F12.wireOp",EDGE,"E12.sketch_text.stroke-40"),sQuery(id+"F12.wireOp",EDGE,"E12.sketch_text.stroke-41"),sQuery(id+"F12.wireOp",EDGE,"E12.sketch_text.stroke-42"),sQuery(id+"F12.wireOp",EDGE,"E12.sketch_text.stroke-43"),sQuery(id+"F12.wireOp",EDGE,"E12.sketch_text.stroke-44"),sQuery(id+"F12.wireOp",EDGE,"E12.sketch_text.stroke-45")])],"isStart":true});
            var Q3;
            Q3=makeQuery(id+"F13.opExtrude","CAP_FACE",FACE,{"disambiguationData":[OSD([sQuery(id+"F12.wireOp",EDGE,"E12.sketch_text.stroke-46"),sQuery(id+"F12.wireOp",EDGE,"E12.sketch_text.stroke-47"),sQuery(id+"F12.wireOp",EDGE,"E12.sketch_text.stroke-48"),sQuery(id+"F12.wireOp",EDGE,"E12.sketch_text.stroke-49"),sQuery(id+"F12.wireOp",EDGE,"E12.sketch_text.stroke-50"),sQuery(id+"F12.wireOp",EDGE,"E12.sketch_text.stroke-51"),sQuery(id+"F12.wireOp",EDGE,"E12.sketch_text.stroke-52"),sQuery(id+"F12.wireOp",EDGE,"E12.sketch_text.stroke-53"),sQuery(id+"F12.wireOp",EDGE,"E12.sketch_text.stroke-54"),sQuery(id+"F12.wireOp",EDGE,"E12.sketch_text.stroke-55"),sQuery(id+"F12.wireOp",EDGE,"E12.sketch_text.stroke-56"),sQuery(id+"F12.wireOp",EDGE,"E12.sketch_text.stroke-57")])],"isStart":true});
            var Q4;
            Q4=makeQuery(id+"F13.opExtrude","CAP_FACE",FACE,{"disambiguationData":[OSD([sQuery(id+"F12.wireOp",EDGE,"E12.sketch_text.stroke-58"),sQuery(id+"F12.wireOp",EDGE,"E12.sketch_text.stroke-59"),sQuery(id+"F12.wireOp",EDGE,"E12.sketch_text.stroke-60"),sQuery(id+"F12.wireOp",EDGE,"E12.sketch_text.stroke-61"),sQuery(id+"F12.wireOp",EDGE,"E12.sketch_text.stroke-62"),sQuery(id+"F12.wireOp",EDGE,"E12.sketch_text.stroke-63"),sQuery(id+"F12.wireOp",EDGE,"E12.sketch_text.stroke-64"),sQuery(id+"F12.wireOp",EDGE,"E12.sketch_text.stroke-65"),sQuery(id+"F12.wireOp",EDGE,"E12.sketch_text.stroke-66"),sQuery(id+"F12.wireOp",EDGE,"E12.sketch_text.stroke-67"),sQuery(id+"F12.wireOp",EDGE,"E12.sketch_text.stroke-68"),sQuery(id+"F12.wireOp",EDGE,"E12.sketch_text.stroke-69"),sQuery(id+"F12.wireOp",EDGE,"E12.sketch_text.stroke-70"),sQuery(id+"F12.wireOp",EDGE,"E12.sketch_text.stroke-71"),sQuery(id+"F12.wireOp",EDGE,"E12.sketch_text.stroke-72"),sQuery(id+"F12.wireOp",EDGE,"E12.sketch_text.stroke-73"),sQuery(id+"F12.wireOp",EDGE,"E12.sketch_text.stroke-74"),sQuery(id+"F12.wireOp",EDGE,"E12.sketch_text.stroke-75"),sQuery(id+"F12.wireOp",EDGE,"E12.sketch_text.stroke-76"),sQuery(id+"F12.wireOp",EDGE,"E12.sketch_text.stroke-77"),sQuery(id+"F12.wireOp",EDGE,"E12.sketch_text.stroke-78"),sQuery(id+"F12.wireOp",EDGE,"E12.sketch_text.stroke-79"),sQuery(id+"F12.wireOp",EDGE,"E12.sketch_text.stroke-80"),sQuery(id+"F12.wireOp",EDGE,"E12.sketch_text.stroke-81"),sQuery(id+"F12.wireOp",EDGE,"E12.sketch_text.stroke-82")])],"isStart":true});
            var Q5;
            Q5=makeQuery(id+"F13.opExtrude","CAP_FACE",FACE,{"disambiguationData":[OSD([sQuery(id+"F12.wireOp",EDGE,"E12.sketch_text.stroke-83"),sQuery(id+"F12.wireOp",EDGE,"E12.sketch_text.stroke-84"),sQuery(id+"F12.wireOp",EDGE,"E12.sketch_text.stroke-85"),sQuery(id+"F12.wireOp",EDGE,"E12.sketch_text.stroke-86"),sQuery(id+"F12.wireOp",EDGE,"E12.sketch_text.stroke-87"),sQuery(id+"F12.wireOp",EDGE,"E12.sketch_text.stroke-88"),sQuery(id+"F12.wireOp",EDGE,"E12.sketch_text.stroke-89"),sQuery(id+"F12.wireOp",EDGE,"E12.sketch_text.stroke-90"),sQuery(id+"F12.wireOp",EDGE,"E12.sketch_text.stroke-91"),sQuery(id+"F12.wireOp",EDGE,"E12.sketch_text.stroke-92"),sQuery(id+"F12.wireOp",EDGE,"E12.sketch_text.stroke-93"),sQuery(id+"F12.wireOp",EDGE,"E12.sketch_text.stroke-94"),sQuery(id+"F12.wireOp",EDGE,"E12.sketch_text.stroke-95"),sQuery(id+"F12.wireOp",EDGE,"E12.sketch_text.stroke-96")])],"isStart":true});
            var Q6;
            Q6=makeQuery(id+"F13.opExtrude","CAP_FACE",FACE,{"disambiguationData":[OSD([sQuery(id+"F12.wireOp",EDGE,"E12.sketch_text.stroke-97"),sQuery(id+"F12.wireOp",EDGE,"E12.sketch_text.stroke-98"),sQuery(id+"F12.wireOp",EDGE,"E12.sketch_text.stroke-99"),sQuery(id+"F12.wireOp",EDGE,"E12.sketch_text.stroke-100"),sQuery(id+"F12.wireOp",EDGE,"E12.sketch_text.stroke-101"),sQuery(id+"F12.wireOp",EDGE,"E12.sketch_text.stroke-102"),sQuery(id+"F12.wireOp",EDGE,"E12.sketch_text.stroke-103"),sQuery(id+"F12.wireOp",EDGE,"E12.sketch_text.stroke-104"),sQuery(id+"F12.wireOp",EDGE,"E12.sketch_text.stroke-105"),sQuery(id+"F12.wireOp",EDGE,"E12.sketch_text.stroke-106"),sQuery(id+"F12.wireOp",EDGE,"E12.sketch_text.stroke-107"),sQuery(id+"F12.wireOp",EDGE,"E12.sketch_text.stroke-108"),sQuery(id+"F12.wireOp",EDGE,"E12.sketch_text.stroke-109"),sQuery(id+"F12.wireOp",EDGE,"E12.sketch_text.stroke-110"),sQuery(id+"F12.wireOp",EDGE,"E12.sketch_text.stroke-111")])],"isStart":true});
            var Q7;
            Q7=makeQuery(id+"F13.opExtrude","CAP_FACE",FACE,{"disambiguationData":[OSD([sQuery(id+"F12.wireOp",EDGE,"E12.sketch_text.stroke-112"),sQuery(id+"F12.wireOp",EDGE,"E12.sketch_text.stroke-113"),sQuery(id+"F12.wireOp",EDGE,"E12.sketch_text.stroke-114"),sQuery(id+"F12.wireOp",EDGE,"E12.sketch_text.stroke-115"),sQuery(id+"F12.wireOp",EDGE,"E12.sketch_text.stroke-116"),sQuery(id+"F12.wireOp",EDGE,"E12.sketch_text.stroke-117"),sQuery(id+"F12.wireOp",EDGE,"E12.sketch_text.stroke-118"),sQuery(id+"F12.wireOp",EDGE,"E12.sketch_text.stroke-119"),sQuery(id+"F12.wireOp",EDGE,"E12.sketch_text.stroke-120"),sQuery(id+"F12.wireOp",EDGE,"E12.sketch_text.stroke-121"),sQuery(id+"F12.wireOp",EDGE,"E12.sketch_text.stroke-122"),sQuery(id+"F12.wireOp",EDGE,"E12.sketch_text.stroke-123"),sQuery(id+"F12.wireOp",EDGE,"E12.sketch_text.stroke-124"),sQuery(id+"F12.wireOp",EDGE,"E12.sketch_text.stroke-125"),sQuery(id+"F12.wireOp",EDGE,"E12.sketch_text.stroke-126"),sQuery(id+"F12.wireOp",EDGE,"E12.sketch_text.stroke-127"),sQuery(id+"F12.wireOp",EDGE,"E12.sketch_text.stroke-128"),sQuery(id+"F12.wireOp",EDGE,"E12.sketch_text.stroke-129"),sQuery(id+"F12.wireOp",EDGE,"E12.sketch_text.stroke-130"),sQuery(id+"F12.wireOp",EDGE,"E12.sketch_text.stroke-131"),sQuery(id+"F12.wireOp",EDGE,"E12.sketch_text.stroke-132"),sQuery(id+"F12.wireOp",EDGE,"E12.sketch_text.stroke-133"),sQuery(id+"F12.wireOp",EDGE,"E12.sketch_text.stroke-134"),sQuery(id+"F12.wireOp",EDGE,"E12.sketch_text.stroke-135"),sQuery(id+"F12.wireOp",EDGE,"E12.sketch_text.stroke-136"),sQuery(id+"F12.wireOp",EDGE,"E12.sketch_text.stroke-137")])],"isStart":true});
            extrude(context, id + "F46", {"entities" : qUnion([Q0, Q1, Q2, Q3, Q4, Q5, Q6, Q7]), "depth" : 2.54 * mm, "offsetDistance" : 25.4 * mm});
        }
        {
            var Q0;
            Q0=makeQuery(id+"F33.opExtrude","CAP_FACE",FACE,{"disambiguationData":[OSD([sQuery(id+"F32.wireOp",EDGE,"E55"),sQuery(id+"F32.wireOp",EDGE,"E56"),sQuery(id+"F32.wireOp",EDGE,"E57")])],"isStart":true});
            extrude(context, id + "F47", {"entities" : qUnion([Q0]), "depth" : 3.3 * mm, "offsetDistance" : 25.4 * mm});
        }
        {
            var Q0;
            Q0=makeQuery(id+"F31.opExtrude","CAP_FACE",FACE,{"disambiguationData":[OSD([sQuery(id+"F30.wireOp",EDGE,"E47"),sQuery(id+"F30.wireOp",EDGE,"E48"),sQuery(id+"F30.wireOp",EDGE,"E49"),sQuery(id+"F30.wireOp",EDGE,"E50")])],"isStart":true});
            extrude(context, id + "F48", {"entities" : qUnion([Q0]), "depth" : 5.08 * mm, "offsetDistance" : 25.4 * mm});
        }
        {
            var Q0;
            Q0=makeQuery(id+"F28.opExtrude","CAP_FACE",FACE,{"disambiguationData":[OSD([sQuery(id+"F27.wireOp",EDGE,"E33"),sQuery(id+"F27.wireOp",EDGE,"E34"),sQuery(id+"F27.wireOp",EDGE,"E35"),sQuery(id+"F27.wireOp",EDGE,"E36")])],"isStart":true});
            extrude(context, id + "F49", {"entities" : qUnion([Q0]), "depth" : 5.08 * mm, "offsetDistance" : 25.4 * mm});
        }
        {
            var Q0;
            Q0=makeQuery(id+"F26.opExtrude","CAP_FACE",FACE,{"disambiguationData":[OSD([sQuery(id+"F25.wireOp",EDGE,"E28"),sQuery(id+"F25.wireOp",EDGE,"E29"),sQuery(id+"F25.wireOp",EDGE,"E30"),sQuery(id+"F25.wireOp",EDGE,"E32")])],"isStart":true});
            extrude(context, id + "F50", {"entities" : qUnion([Q0]), "depth" : 5.08 * mm, "offsetDistance" : 25.4 * mm});
        }
        {
            var Q0;
            Q0=makeQuery(id+"F33.opExtrude","CAP_FACE",FACE,{"disambiguationData":[OSD([sQuery(id+"F32.wireOp",EDGE,"E58"),sQuery(id+"F32.wireOp",EDGE,"E59"),sQuery(id+"F32.wireOp",EDGE,"E60")])],"isStart":true});
            extrude(context, id + "F51", {"entities" : qUnion([Q0]), "depth" : 3.3 * mm, "offsetDistance" : 25.4 * mm});
        }
        {
            var Q0;
            Q0=makeQuery(id+"F31.opExtrude","CAP_FACE",FACE,{"disambiguationData":[OSD([sQuery(id+"F30.wireOp",EDGE,"E51"),sQuery(id+"F30.wireOp",EDGE,"E52"),sQuery(id+"F30.wireOp",EDGE,"E53"),sQuery(id+"F30.wireOp",EDGE,"E54")])],"isStart":true});
            extrude(context, id + "F52", {"entities" : qUnion([Q0]), "depth" : 5.08 * mm, "offsetDistance" : 25.4 * mm});
        }
        {
            var Q0;
            Q0=makeQuery(id+"F28.opExtrude","CAP_FACE",FACE,{"disambiguationData":[OSD([sQuery(id+"F27.wireOp",EDGE,"E37"),sQuery(id+"F27.wireOp",EDGE,"E38"),sQuery(id+"F27.wireOp",EDGE,"E39"),sQuery(id+"F27.wireOp",EDGE,"E40")])],"isStart":true});
            extrude(context, id + "F53", {"entities" : qUnion([Q0]), "depth" : 5.08 * mm, "offsetDistance" : 25.4 * mm});
        }
        {
            var Q0;
            Q0=makeQuery(id+"F26.opExtrude","CAP_FACE",FACE,{"disambiguationData":[OSD([sQuery(id+"F25.wireOp",EDGE,"E25"),sQuery(id+"F25.wireOp",EDGE,"E26"),sQuery(id+"F25.wireOp",EDGE,"E27"),sQuery(id+"F25.wireOp",EDGE,"E31")])],"isStart":true});
            extrude(context, id + "F54", {"entities" : qUnion([Q0]), "depth" : 5.08 * mm, "offsetDistance" : 25.4 * mm});
        }
        {
            var Q0;
            Q0=makeQuery(id+"F35.opExtrude","CAP_FACE",FACE,{"disambiguationData":[OSD([sQuery(id+"F34.wireOp",EDGE,"E61"),sQuery(id+"F34.wireOp",EDGE,"E62"),sQuery(id+"F34.wireOp",EDGE,"E63"),sQuery(id+"F34.wireOp",EDGE,"E64")])],"isStart":true});
            extrude(context, id + "F55", {"entities" : qUnion([Q0]), "operationType" : NewBodyOperationType.ADD, "depth" : 5.08 * mm, "offsetDistance" : 25.4 * mm});
        }
        {
            var Q0;
            Q0=makeQuery(id+"F43.opExtrude","CAP_FACE",FACE,{"disambiguationData":[OSD([sQuery(id+"F36.wireOp",EDGE,"E73"),sQuery(id+"F36.wireOp",EDGE,"E74"),sQuery(id+"F36.wireOp",EDGE,"E75"),sQuery(id+"F36.wireOp",EDGE,"E76")])],"isStart":true});
            extrude(context, id + "F56", {"entities" : qUnion([Q0]), "depth" : 5.08 * mm, "offsetDistance" : 25.4 * mm});
        }
        {
            var Q0;
            Q0=makeQuery(id+"F35.opExtrude","CAP_FACE",FACE,{"disambiguationData":[OSD([sQuery(id+"F34.wireOp",EDGE,"E65"),sQuery(id+"F34.wireOp",EDGE,"E66"),sQuery(id+"F34.wireOp",EDGE,"E67"),sQuery(id+"F34.wireOp",EDGE,"E68")])],"isStart":true});
            extrude(context, id + "F57", {"entities" : qUnion([Q0]), "operationType" : NewBodyOperationType.ADD, "depth" : 5.08 * mm, "offsetDistance" : 25.4 * mm});
        }
        {
            var Q0;
            Q0=makeQuery(id+"F43.opExtrude","CAP_FACE",FACE,{"disambiguationData":[OSD([sQuery(id+"F36.wireOp",EDGE,"E69"),sQuery(id+"F36.wireOp",EDGE,"E70"),sQuery(id+"F36.wireOp",EDGE,"E71"),sQuery(id+"F36.wireOp",EDGE,"E72")])],"isStart":true});
            extrude(context, id + "F58", {"entities" : qUnion([Q0]), "depth" : 5.08 * mm, "offsetDistance" : 25.4 * mm});
        }
        {
            var Q0;
            Q0=makeQuery(id+"F28.opExtrude","CAP_EDGE",EDGE,{"disambiguationData":[OSD([sQuery(id+"F27.wireOp",EDGE,"E38")])],"isStart":false});
            var Q1;
            Q1=makeQuery(id+"F31.opExtrude","CAP_EDGE",EDGE,{"disambiguationData":[OSD([sQuery(id+"F30.wireOp",EDGE,"E52")])],"isStart":false});
            var Q2;
            Q2=makeQuery(id+"F31.opExtrude","CAP_EDGE",EDGE,{"disambiguationData":[OSD([sQuery(id+"F30.wireOp",EDGE,"E54")])],"isStart":false});
            var Q3;
            Q3=makeQuery(id+"F26.opExtrude","CAP_EDGE",EDGE,{"disambiguationData":[OSD([sQuery(id+"F25.wireOp",EDGE,"E27")])],"isStart":false});
            var Q4;
            Q4=makeQuery(id+"F26.opExtrude","CAP_EDGE",EDGE,{"disambiguationData":[OSD([sQuery(id+"F25.wireOp",EDGE,"E30")])],"isStart":false});
            var Q5;
            Q5=makeQuery(id+"F28.opExtrude","CAP_EDGE",EDGE,{"disambiguationData":[OSD([sQuery(id+"F27.wireOp",EDGE,"E34")])],"isStart":false});
            var Q6;
            Q6=makeQuery(id+"F31.opExtrude","CAP_EDGE",EDGE,{"disambiguationData":[OSD([sQuery(id+"F30.wireOp",EDGE,"E47")])],"isStart":false});
            var Q7;
            Q7=makeQuery(id+"F31.opExtrude","CAP_EDGE",EDGE,{"disambiguationData":[OSD([sQuery(id+"F30.wireOp",EDGE,"E49")])],"isStart":false});
            var Q8;
            Q8=makeQuery(id+"F35.opExtrude","CAP_EDGE",EDGE,{"disambiguationData":[OSD([sQuery(id+"F34.wireOp",EDGE,"E61")])],"isStart":false});
            var Q9;
            Q9=makeQuery(id+"F43.opExtrude","CAP_EDGE",EDGE,{"disambiguationData":[OSD([sQuery(id+"F36.wireOp",EDGE,"E74")])],"isStart":false});
            var Q10;
            Q10=makeQuery(id+"F43.opExtrude","CAP_EDGE",EDGE,{"disambiguationData":[OSD([sQuery(id+"F36.wireOp",EDGE,"E70")])],"isStart":false});
            var Q11;
            Q11=makeQuery(id+"F35.opExtrude","CAP_EDGE",EDGE,{"disambiguationData":[OSD([sQuery(id+"F34.wireOp",EDGE,"E68")])],"isStart":false});
            var Q12;
            Q12=makeQuery(id+"F49.opExtrude","CAP_EDGE",EDGE,{"disambiguationData":[OSD([sQuery(id+"F27.wireOp",EDGE,"E34")])],"isStart":false});
            var Q13;
            Q13=makeQuery(id+"F53.opExtrude","CAP_EDGE",EDGE,{"disambiguationData":[OSD([sQuery(id+"F27.wireOp",EDGE,"E38")])],"isStart":false});
            var Q14;
            Q14=makeQuery(id+"F57.opExtrude","CAP_EDGE",EDGE,{"disambiguationData":[OSD([sQuery(id+"F34.wireOp",EDGE,"E68")])],"isStart":false});
            var Q15;
            Q15=makeQuery(id+"F58.opExtrude","CAP_EDGE",EDGE,{"disambiguationData":[OSD([sQuery(id+"F36.wireOp",EDGE,"E70")])],"isStart":false});
            var Q16;
            Q16=makeQuery(id+"F56.opExtrude","CAP_EDGE",EDGE,{"disambiguationData":[OSD([sQuery(id+"F36.wireOp",EDGE,"E74")])],"isStart":false});
            var Q17;
            Q17=makeQuery(id+"F55.opExtrude","CAP_EDGE",EDGE,{"disambiguationData":[OSD([sQuery(id+"F34.wireOp",EDGE,"E61")])],"isStart":false});
            var Q18;
            Q18=makeQuery(id+"F54.opExtrude","CAP_EDGE",EDGE,{"disambiguationData":[OSD([sQuery(id+"F25.wireOp",EDGE,"E27")])],"isStart":false});
            var Q19;
            Q19=makeQuery(id+"FyTuqV0zrKyyp0G_29.opExtrude","CAP_EDGE",EDGE,{"disambiguationData":[OSD([sQuery(id+"FDzdp0wdTou221i_29.wireOp",EDGE,"NCpSs36h-GLtG-e2i8-rEVY-aWUY7J7raK3y")])],"isStart":false});
            var Q20;
            Q20=makeQuery(id+"FyTuqV0zrKyyp0G_29.opExtrude","CAP_EDGE",EDGE,{"disambiguationData":[OSD([sQuery(id+"FDzdp0wdTou221i_29.wireOp",EDGE,"cpbqBVkj-bqiv-rwLY-j3fs-Z4UFoXbcNN4h")])],"isStart":false});
            var Q21;
            Q21=makeQuery(id+"FyTuqV0zrKyyp0G_29.opExtrude","CAP_EDGE",EDGE,{"disambiguationData":[OSD([sQuery(id+"FDzdp0wdTou221i_29.wireOp",EDGE,"8LbKEtTS-qgaQ-0bYv-YJTT-WaLf3WoMZucl")])],"isStart":false});
            var Q22;
            Q22=makeQuery(id+"FyTuqV0zrKyyp0G_29.opExtrude","CAP_EDGE",EDGE,{"disambiguationData":[OSD([sQuery(id+"FDzdp0wdTou221i_29.wireOp",EDGE,"I2cjMhAN-swzq-isOR-Jg6F-DYy2kZu2BvA6")])],"isStart":false});
            var Q23;
            Q23=makeQuery(id+"FLcrFYpG1scf5mV_63.opExtrude","CAP_EDGE",EDGE,{"disambiguationData":[OSD([sQuery(id+"FDzdp0wdTou221i_29.wireOp",EDGE,"I2cjMhAN-swzq-isOR-Jg6F-DYy2kZu2BvA6")])],"isStart":false});
            var Q24;
            Q24=makeQuery(id+"FLcrFYpG1scf5mV_63.opExtrude","CAP_EDGE",EDGE,{"disambiguationData":[OSD([sQuery(id+"FDzdp0wdTou221i_29.wireOp",EDGE,"8LbKEtTS-qgaQ-0bYv-YJTT-WaLf3WoMZucl")])],"isStart":false});
            var Q25;
            Q25=makeQuery(id+"FaaUI9km4A5iTYL_66.opExtrude","CAP_EDGE",EDGE,{"disambiguationData":[OSD([sQuery(id+"FDzdp0wdTou221i_29.wireOp",EDGE,"cpbqBVkj-bqiv-rwLY-j3fs-Z4UFoXbcNN4h")])],"isStart":false});
            var Q26;
            Q26=makeQuery(id+"FaaUI9km4A5iTYL_66.opExtrude","CAP_EDGE",EDGE,{"disambiguationData":[OSD([sQuery(id+"FDzdp0wdTou221i_29.wireOp",EDGE,"NCpSs36h-GLtG-e2i8-rEVY-aWUY7J7raK3y")])],"isStart":false});
            var Q27;
            Q27=makeQuery(id+"F48.opExtrude","CAP_EDGE",EDGE,{"disambiguationData":[OSD([sQuery(id+"F30.wireOp",EDGE,"E47")])],"isStart":false});
            var Q28;
            Q28=makeQuery(id+"F48.opExtrude","CAP_EDGE",EDGE,{"disambiguationData":[OSD([sQuery(id+"F30.wireOp",EDGE,"E49")])],"isStart":false});
            var Q29;
            Q29=makeQuery(id+"F48.opExtrude","CAP_EDGE",EDGE,{"disambiguationData":[OSD([sQuery(id+"F30.wireOp",EDGE,"E48")])],"isStart":false});
            var Q30;
            Q30=makeQuery(id+"F52.opExtrude","CAP_EDGE",EDGE,{"disambiguationData":[OSD([sQuery(id+"F30.wireOp",EDGE,"E52")])],"isStart":false});
            var Q31;
            Q31=makeQuery(id+"F52.opExtrude","CAP_EDGE",EDGE,{"disambiguationData":[OSD([sQuery(id+"F30.wireOp",EDGE,"E54")])],"isStart":false});
            var Q32;
            Q32=makeQuery(id+"F52.opExtrude","CAP_EDGE",EDGE,{"disambiguationData":[OSD([sQuery(id+"F30.wireOp",EDGE,"E53")])],"isStart":false});
            var Q33;
            Q33=makeQuery(id+"F31.opExtrude","CAP_EDGE",EDGE,{"disambiguationData":[OSD([sQuery(id+"F30.wireOp",EDGE,"E53")])],"isStart":false});
            var Q34;
            Q34=makeQuery(id+"F31.opExtrude","CAP_EDGE",EDGE,{"disambiguationData":[OSD([sQuery(id+"F30.wireOp",EDGE,"E48")])],"isStart":false});
            var Q35;
            Q35=makeQuery(id+"F50.opExtrude","CAP_EDGE",EDGE,{"disambiguationData":[OSD([sQuery(id+"F25.wireOp",EDGE,"E30")])],"isStart":false});
            chamfer(context, id + "F59", {"entities" : qUnion([Q0, Q1, Q2, Q3, Q4, Q5, Q6, Q7, Q8, Q9, Q10, Q11, Q12, Q13, Q14, Q15, Q16, Q17, Q18, Q19, Q20, Q21, Q22, Q23, Q24, Q25, Q26, Q27, Q28, Q29, Q30, Q31, Q32, Q33, Q34, Q35]), "width" : 1.78 * mm, "tangentPropagation" : true});
        }
        {
            var Q0;
            Q0=makeQuery(id+"F0.imprint","IMPRINT",FACE,{"disambiguationData":[TD([[makeQuery(id+"F0.imprint","IMPRINT",EDGE,{"derivedFrom":sQuery(id+"F0.wireOp",EDGE,"E0.bottom")}),-1.0]])]});
            extrude(context, id + "F60", {"entities" : qUnion([Q0]), "operationType" : NewBodyOperationType.REMOVE, "depth" : 25.4 * mm, "offsetDistance" : 25.4 * mm});
        }
        {
            var Q0;
            Q0=makeQuery(id+"F0.imprint","IMPRINT",FACE,{"disambiguationData":[TD([[makeQuery(id+"F0.imprint","IMPRINT",EDGE,{"derivedFrom":sQuery(id+"F0.wireOp",EDGE,"E0.bottom")}),-1.0]])]});
            extrude(context, id + "F61", {"entities" : qUnion([Q0]), "depth" : 2.54 * mm, "offsetDistance" : 25.4 * mm});
        }
        {
            var Q0;
            Q0=makeQuery(id+"F58.opExtrude","SWEPT_FACE",FACE,{"disambiguationData":[OSD([sQuery(id+"F36.wireOp",EDGE,"E69")])]});
            cPlane(context, id + "F62", {"entities" : qUnion([Q0]), "cplaneType" : CPlaneType.OFFSET, "offset" : 0 * mm, "width" : 152.4 * mm, "height" : 152.4 * mm});
        }
        {
            var Q0;
            Q0=qCreatedBy(id+"F62.planeOp",FACE);
            var sketch = newSketch(context, id + "F63", { "sketchPlane" : qUnion([Q0])});
            skCircle(sketch, "E125.cCircle", {"center": v(-0.45, 2.54) * mm, "radius": 3.94 * mm, "construction": true});
            skLineSegment(sketch, "E125.0", {"start": v(4.1, 2.54) * mm, "end": v(1.82, -1.4) * mm});
            skLineSegment(sketch, "E125.1", {"start": v(1.82, -1.4) * mm, "end": v(-2.72, -1.4) * mm});
            skLineSegment(sketch, "E125.2", {"start": v(-2.72, -1.4) * mm, "end": v(-5, 2.54) * mm});
            skLineSegment(sketch, "E125.3", {"start": v(-5, 2.54) * mm, "end": v(-2.72, 6.48) * mm});
            skLineSegment(sketch, "E125.4", {"start": v(-2.72, 6.48) * mm, "end": v(1.82, 6.48) * mm});
            skLineSegment(sketch, "E125.5", {"start": v(1.82, 6.48) * mm, "end": v(4.1, 2.54) * mm});
            skPoint(sketch, "E125.0.midPoint", {"position": v(2.96, 0.57) * mm});
            skSolve(sketch);
        }
        {
            var Q0;
            Q0=makeQuery(id+"F63.imprint","IMPRINT",FACE,{"disambiguationData":[TD([[makeQuery(id+"F63.imprint","IMPRINT",EDGE,{"derivedFrom":sQuery(id+"F63.wireOp",EDGE,"E125.0")}),-1.0]])]});
            extrude(context, id + "F64", {"entities" : qUnion([Q0]), "oppositeDirection" : true, "depth" : 63.5 * mm, "offsetDistance" : 25.4 * mm, "hasSecondDirection" : true, "secondDirectionOppositeDirection" : true, "secondDirectionDepth" : 6.35 * mm});
        }
        {
            var Q0;
            Q0=qCreatedBy(id+"F40.planeOp",FACE);
            var sketch = newSketch(context, id + "F65", { "sketchPlane" : qUnion([Q0])});
            skLineSegment(sketch, "E126", {"start": v(-24.42, 25.05) * mm, "end": v(-7.25, 20.45) * mm});
            skLineSegment(sketch, "E127", {"start": v(-7.25, 20.45) * mm, "end": v(-19.82, 33.02) * mm});
            skLineSegment(sketch, "E128", {"start": v(-19.82, 33.02) * mm, "end": v(-26.1, 26.74) * mm});
            skLineSegment(sketch, "E129", {"start": v(-26.1, 26.74) * mm, "end": v(-24.42, 25.05) * mm});
            skLineSegment(sketch, "E130", {"start": v(-26.1, 26.74) * mm, "end": v(-33.29, 33.92) * mm});
            skSolve(sketch);
        }
        {
            var Q0;
            Q0=makeQuery(id+"F65.imprint","IMPRINT",FACE,{"disambiguationData":[TD([[makeQuery(id+"F65.imprint","IMPRINT",EDGE,{"derivedFrom":sQuery(id+"F65.wireOp",EDGE,"E126")}),1.0]])]});
            var Q1;
            Q1=sQuery(id+"F65.wireOp",EDGE,"E130");
            revolve(context, id + "F66", {"operationType" : NewBodyOperationType.REMOVE, "surfaceOperationType" : NewSurfaceOperationType.NEW, "entities" : qUnion([Q0]), "axis" : qUnion([Q1]), "revolveType" : RevolveType.FULL});
        }
        {
            var Q0;
            Q0=makeQuery(id+"F61.opExtrude","CAP_FACE",FACE,{"disambiguationData":[OSD([sQuery(id+"F0.wireOp",EDGE,"E0.bottom"),sQuery(id+"F0.wireOp",EDGE,"E0.top"),sQuery(id+"F0.wireOp",EDGE,"E0.left"),sQuery(id+"F0.wireOp",EDGE,"E0.right")])],"isStart":false});
            extrude(context, id + "F67", {"entities" : qUnion([Q0]), "operationType" : NewBodyOperationType.REMOVE, "depth" : 25.4 * mm, "offsetDistance" : 25.4 * mm});
        }
        {
            var Q0;
            Q0=makeQuery(id+"F9.opExtrude","CAP_FACE",FACE,{"disambiguationData":[OSD([sQuery(id+"F0.wireOp",EDGE,"E0.bottom"),sQuery(id+"F8.wireOp",EDGE,"E10")])],"isStart":true});
            extrude(context, id + "F68", {"entities" : qUnion([Q0]), "depth" : 3.05 * mm, "offsetDistance" : 25.4 * mm});
        }
        {
            var Q0;
            Q0=makeQuery(id+"F64.opExtrude","CAP_FACE",FACE,{"disambiguationData":[OSD([sQuery(id+"F63.wireOp",EDGE,"E125.0"),sQuery(id+"F63.wireOp",EDGE,"E125.1"),sQuery(id+"F63.wireOp",EDGE,"E125.2"),sQuery(id+"F63.wireOp",EDGE,"E125.3"),sQuery(id+"F63.wireOp",EDGE,"E125.4"),sQuery(id+"F63.wireOp",EDGE,"E125.5")])],"isStart":true});
            var sketch = newSketch(context, id + "F69", { "sketchPlane" : qUnion([Q0])});
            skCircle(sketch, "E131", {"center": v(-0.45, 2.54) * mm, "radius": 3.94 * mm, "construction": true});
            skCircle(sketch, "E132.0", {"center": v(-0.45, 2.54) * mm, "radius": 4.57 * mm});
            skLineSegment(sketch, "E133.0", {"start": v(-44.52, -6.35) * mm, "end": v(57.99, -6.35) * mm});
            skLineSegment(sketch, "E133.1", {"start": v(-44.52, 8.9) * mm, "end": v(-44.52, -6.35) * mm});
            skLineSegment(sketch, "E133.2", {"start": v(57.99, 8.9) * mm, "end": v(-44.52, 8.9) * mm});
            skLineSegment(sketch, "E133.3", {"start": v(57.99, -6.35) * mm, "end": v(57.99, 8.9) * mm});
            skSolve(sketch);
        }
        {
            var Q0;
            Q0=makeQuery(id+"F69.imprint","IMPRINT",FACE,{"disambiguationData":[TD([[makeQuery(id+"F69.imprint","IMPRINT",EDGE,{"derivedFrom":sQuery(id+"F69.wireOp",EDGE,"E132.0")}),1.0]])]});
            var Q1;
            Q1=makeQuery(id+"F69.imprint","IMPRINT",FACE,{"disambiguationData":[TD([[makeQuery(id+"F69.imprint","IMPRINT",EDGE,{"derivedFrom":makeQuery(id+"F64.opExtrude","CAP_EDGE",EDGE,{"disambiguationData":[OSD([sQuery(id+"F63.wireOp",EDGE,"E125.0")])],"isStart":true})}),-1.0]])]});
            extrude(context, id + "F70", {"entities" : qUnion([Q0, Q1]), "operationType" : NewBodyOperationType.ADD, "depth" : 5.08 * mm, "offsetDistance" : 25.4 * mm});
        }
        {
            var Q0;
            Q0=makeQuery(id+"F39.opExtrude","CAP_FACE",FACE,{"disambiguationData":[OSD([sQuery(id+"F38.wireOp",EDGE,"E77.0"),sQuery(id+"F38.wireOp",EDGE,"E77.1"),sQuery(id+"F38.wireOp",EDGE,"E77.2"),sQuery(id+"F38.wireOp",EDGE,"E77.3"),sQuery(id+"F38.wireOp",EDGE,"E77.4"),sQuery(id+"F38.wireOp",EDGE,"E77.5")])],"isStart":true});
            var sketch = newSketch(context, id + "F71", { "sketchPlane" : qUnion([Q0])});
            skCircle(sketch, "E134", {"center": v(-2.54, 0.45) * mm, "radius": 3.94 * mm, "construction": true});
            skCircle(sketch, "E135.0", {"center": v(-2.54, 0.45) * mm, "radius": 4.57 * mm});
            skSolve(sketch);
        }
        {
            var Q0;
            Q0 = qSketchRegion(id + "F71", true);
            extrude(context, id + "F72", {"entities" : qUnion([Q0]), "operationType" : NewBodyOperationType.ADD, "depth" : 5.08 * mm, "offsetDistance" : 25.4 * mm});
        }
        {
            var Q0;
            Q0=makeQuery(id+"F61.opExtrude","CAP_FACE",FACE,{"disambiguationData":[OSD([sQuery(id+"F0.wireOp",EDGE,"E0.bottom"),sQuery(id+"F0.wireOp",EDGE,"E0.top"),sQuery(id+"F0.wireOp",EDGE,"E0.left"),sQuery(id+"F0.wireOp",EDGE,"E0.right")])],"isStart":true});
            extrude(context, id + "F73", {"entities" : qUnion([Q0]), "operationType" : NewBodyOperationType.REMOVE, "depth" : 25.4 * mm, "offsetDistance" : 25.4 * mm});
        }
    });
